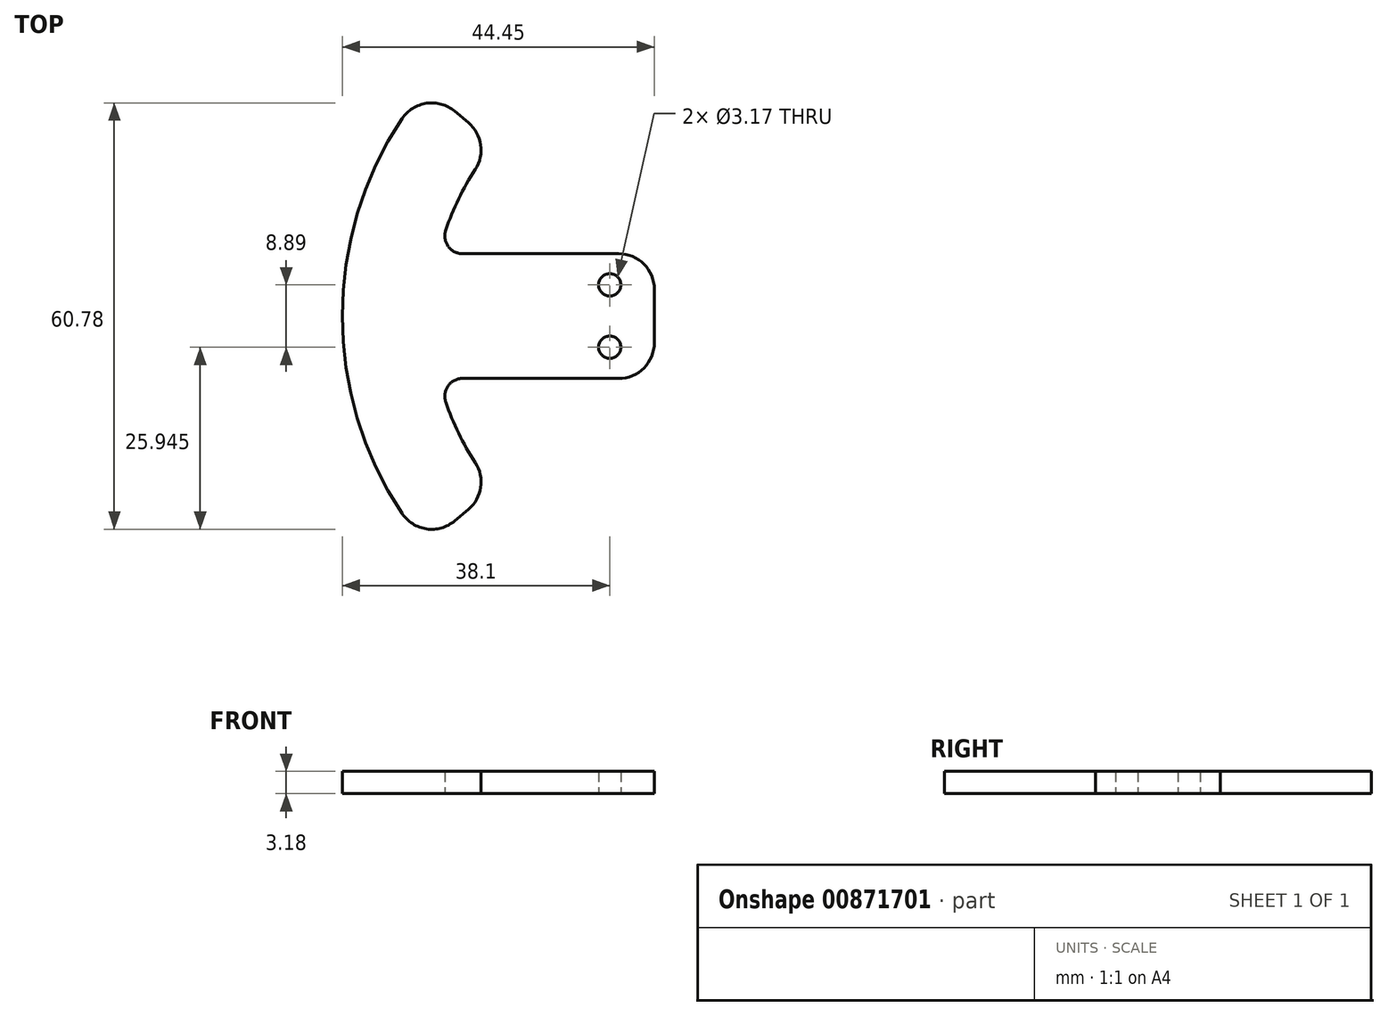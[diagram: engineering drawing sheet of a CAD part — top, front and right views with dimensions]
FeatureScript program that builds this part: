
annotation { "Feature Type Name" : "Feature", "Feature Type Description" : "" }
export const myFeature = defineFeature(function(context is Context, id is Id, definition is map)
    precondition{}
    {
        {
            var Q0;
            Q0=qCreatedBy(makeId("Top.planeOp"),FACE);
            var sketch = newSketch(context, id + "F0", { "sketchPlane" : qUnion([Q0])});
            skArc(sketch, "E0", {"start": v(-38.92, -32.65) * mm, "mid": v(-47.74, -17.37) * mm, "end": v(-50.8, 0) * mm});
            skArc(sketch, "E1", {"start": v(-29.19, -24.5) * mm, "mid": v(-34.02, -17.15) * mm, "end": v(-37.05, -8.89) * mm});
            skLineSegment(sketch, "E2", {"start": v(-29.19, -24.5) * mm, "end": v(-38.92, -32.65) * mm});
            skLineSegment(sketch, "E3", {"start": v(0, 0) * mm, "end": v(-25.5, -21.39) * mm, "construction": true});
            skArc(sketch, "E4.MirrorCS", {"start": v(-38.92, 32.65) * mm, "mid": v(-47.74, 17.37) * mm, "end": v(-50.8, 0) * mm});
            skArc(sketch, "E5.MirrorCS", {"start": v(-29.19, 24.5) * mm, "mid": v(-34.02, 17.15) * mm, "end": v(-37.05, 8.89) * mm});
            skLineSegment(sketch, "E6.MirrorCS", {"start": v(-29.19, 24.5) * mm, "end": v(-38.92, 32.65) * mm});
            skCircle(sketch, "E7", {"center": v(-12.7, -4.45) * mm, "radius": 1.59 * mm});
            skCircle(sketch, "E8.MirrorC", {"center": v(-12.7, 4.45) * mm, "radius": 1.59 * mm});
            skLineSegment(sketch, "E9", {"start": v(-37.05, -8.9) * mm, "end": v(-6.35, -8.9) * mm});
            skLineSegment(sketch, "E10", {"start": v(-6.35, -8.9) * mm, "end": v(-6.35, 0) * mm});
            skLineSegment(sketch, "E11.MirrorCS", {"start": v(-37.05, 8.89) * mm, "end": v(-6.35, 8.9) * mm});
            skLineSegment(sketch, "E12.MirrorCS", {"start": v(-6.35, 8.9) * mm, "end": v(-6.35, 0) * mm});
            skSolve(sketch);
        }
        {
            var Q0;
            Q0 = qSketchRegion(id + "F0", true);
            extrude(context, id + "F1", {"entities" : qUnion([Q0]), "depth" : 3.17 * mm, "offsetDistance" : 25.4 * mm});
        }
        {
            var Q0;
            Q0=makeQuery(id+"F1.opExtrude","SWEPT_EDGE",EDGE,{"disambiguationData":[OSD([sQuery(id+"F0.wireOp",EDGE,"E4.MirrorCS"),sQuery(id+"F0.wireOp",EDGE,"E6.MirrorCS")])]});
            var Q1;
            Q1=makeQuery(id+"F1.opExtrude","SWEPT_EDGE",EDGE,{"disambiguationData":[OSD([sQuery(id+"F0.wireOp",EDGE,"E0"),sQuery(id+"F0.wireOp",EDGE,"E2")])]});
            fillet(context, id + "F2", {"entities" : qUnion([Q0, Q1]), "radius" : 5.08 * mm, "tangentPropagation" : true, "allowEdgeOverflow" : false});
        }
        {
            var Q0;
            Q0=makeQuery(id+"F1.opExtrude","SWEPT_EDGE",EDGE,{"disambiguationData":[OSD([sQuery(id+"F0.wireOp",EDGE,"E5.MirrorCS"),sQuery(id+"F0.wireOp",EDGE,"E6.MirrorCS")])]});
            var Q1;
            Q1=makeQuery(id+"F1.opExtrude","SWEPT_EDGE",EDGE,{"disambiguationData":[OSD([sQuery(id+"F0.wireOp",EDGE,"E1"),sQuery(id+"F0.wireOp",EDGE,"E2")])]});
            fillet(context, id + "F3", {"entities" : qUnion([Q0, Q1]), "radius" : 5.08 * mm, "tangentPropagation" : true, "allowEdgeOverflow" : false});
        }
        {
            var Q0;
            Q0=makeQuery(id+"F1.opExtrude","SWEPT_EDGE",EDGE,{"disambiguationData":[OSD([sQuery(id+"F0.wireOp",EDGE,"E1"),sQuery(id+"F0.wireOp",EDGE,"Pnl9IDrL-oQaz-SCvt-UswR-xG0UkwfoS7ud")])]});
            var Q1;
            Q1=makeQuery(id+"F1.opExtrude","SWEPT_EDGE",EDGE,{"disambiguationData":[OSD([sQuery(id+"F0.wireOp",EDGE,"E5.MirrorCS"),sQuery(id+"F0.wireOp",EDGE,"14e6f9a3-2757-45bb-853b-ee2c686c86ed0.MirrorCS")])]});
            fillet(context, id + "F4", {"entities" : qUnion([Q0, Q1]), "radius" : 2.54 * mm, "tangentPropagation" : true, "allowEdgeOverflow" : false});
        }
        {
            var Q0;
            Q0=makeQuery(id+"F1.opExtrude","SWEPT_EDGE",EDGE,{"disambiguationData":[OSD([sQuery(id+"F0.wireOp",EDGE,"E11.MirrorCS"),sQuery(id+"F0.wireOp",EDGE,"E12.MirrorCS")])]});
            var Q1;
            Q1=makeQuery(id+"F1.opExtrude","SWEPT_EDGE",EDGE,{"disambiguationData":[OSD([sQuery(id+"F0.wireOp",EDGE,"E9"),sQuery(id+"F0.wireOp",EDGE,"E10")])]});
            fillet(context, id + "F5", {"entities" : qUnion([Q0, Q1]), "radius" : 5.08 * mm, "tangentPropagation" : true, "allowEdgeOverflow" : false});
        }
    });
